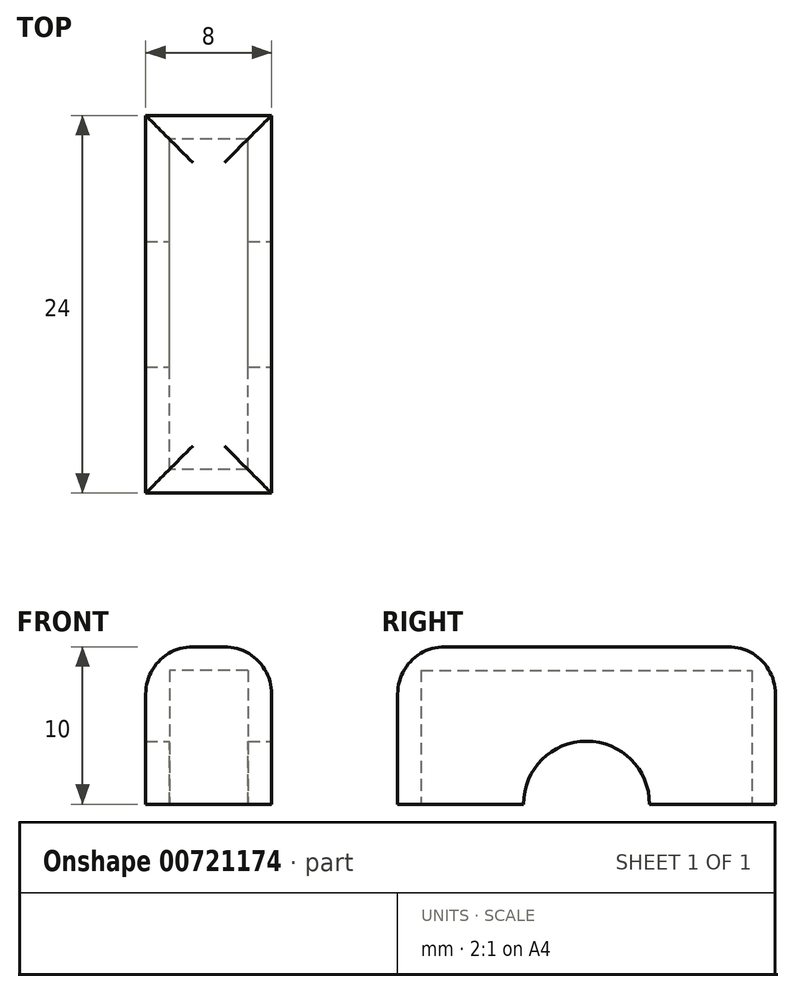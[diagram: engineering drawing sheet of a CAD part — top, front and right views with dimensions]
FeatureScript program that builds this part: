
annotation { "Feature Type Name" : "Feature", "Feature Type Description" : "" }
export const myFeature = defineFeature(function(context is Context, id is Id, definition is map)
    precondition{}
    {
        {
            var Q0;
            Q0=qCreatedBy(makeId("Top.planeOp"),FACE);
            var sketch = newSketch(context, id + "F0", { "sketchPlane" : qUnion([Q0])});
            skLineSegment(sketch, "E0.bottom", {"start": v(4, -12) * mm, "end": v(-4, -12) * mm});
            skLineSegment(sketch, "E0.top", {"start": v(4, 12) * mm, "end": v(-4, 12) * mm});
            skLineSegment(sketch, "E0.left", {"start": v(4, -12) * mm, "end": v(4, 12) * mm});
            skLineSegment(sketch, "E0.right", {"start": v(-4, -12) * mm, "end": v(-4, 12) * mm});
            skPoint(sketch, "E0.middle", {"position": v(0, 0) * mm});
            skPoint(sketch, "E1", {"position": v(4, 0) * mm});
            skPoint(sketch, "E2", {"position": v(-4, 0) * mm});
            skSolve(sketch);
        }
        {
            var Q0;
            Q0=makeQuery(id+"F0.imprint","IMPRINT",FACE,{"disambiguationData":[TD([[makeQuery(id+"F0.imprint","IMPRINT",EDGE,{"derivedFrom":sQuery(id+"F0.wireOp",EDGE,"E0.bottom")}),-1.0]])]});
            extrude(context, id + "F1", {"entities" : qUnion([Q0]), "depth" : 10 * mm, "offsetDistance" : 25.4 * mm});
        }
        {
            var Q0;
            Q0=makeQuery(id+"F1.opExtrude","CAP_FACE",FACE,{"disambiguationData":[OSD([sQuery(id+"F0.wireOp",EDGE,"E0.bottom"),sQuery(id+"F0.wireOp",EDGE,"E0.top"),sQuery(id+"F0.wireOp",EDGE,"E0.left"),sQuery(id+"F0.wireOp",EDGE,"E0.right")])],"isStart":true});
            shell(context, id + "F2", {"entities" : qUnion([Q0]), "thickness" : 1.5 * mm});
        }
        {
            var Q0;
            Q0=makeQuery(id+"F1.opExtrude","SWEPT_FACE",FACE,{"disambiguationData":[OSD([sQuery(id+"F0.wireOp",EDGE,"E0.left")])]});
            var sketch = newSketch(context, id + "F3", { "sketchPlane" : qUnion([Q0])});
            skPoint(sketch, "E3", {"position": v(0, 0) * mm});
            skSolve(sketch);
        }
        {
            var Q0;
            Q0=sQuery(id+"F3.wireOp",VERTEX,"E3");
            var Q1;
            Q1=makeQuery(id+"F1.opExtrude","SWEPT_BODY",BODY,{"disambiguationData":[OSD([sQuery(id+"F0.wireOp",EDGE,"E0.bottom"),sQuery(id+"F0.wireOp",EDGE,"E0.top"),sQuery(id+"F0.wireOp",EDGE,"E0.left"),sQuery(id+"F0.wireOp",EDGE,"E0.right")])]});
            hole(context, id + "F4", {"style" : HoleStyle.SIMPLE, "endStyle" : HoleEndStyle.THROUGH, "holeDiameter" : 8 * mm, "majorDiameter" : 6.35 * mm, "isTappedThrough" : true, "tappedDepth" : 12.7 * mm, "tapClearance" : 3, "locations" : qUnion([Q0]), "scope" : qUnion([Q1])});
        }
        {
            var Q0;
            Q0=makeQuery(id+"F1.opExtrude","CAP_FACE",FACE,{"disambiguationData":[OSD([sQuery(id+"F0.wireOp",EDGE,"E0.bottom"),sQuery(id+"F0.wireOp",EDGE,"E0.top"),sQuery(id+"F0.wireOp",EDGE,"E0.left"),sQuery(id+"F0.wireOp",EDGE,"E0.right")])],"isStart":false});
            fillet(context, id + "F5", {"entities" : qUnion([Q0]), "radius" : 3 * mm, "tangentPropagation" : true, "allowEdgeOverflow" : false});
        }
    });
